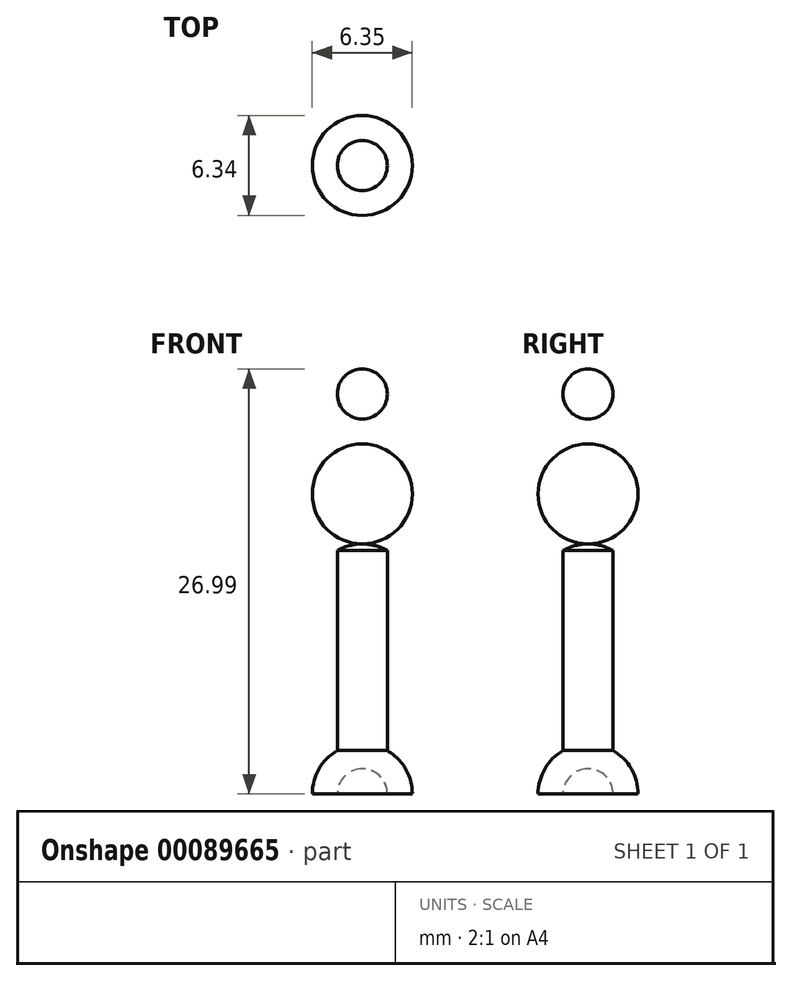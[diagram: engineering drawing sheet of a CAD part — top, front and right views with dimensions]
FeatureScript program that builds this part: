
annotation { "Feature Type Name" : "Feature", "Feature Type Description" : "" }
export const myFeature = defineFeature(function(context is Context, id is Id, definition is map)
    precondition{}
    {
        {
            var Q0;
            Q0=qCreatedBy(makeId("Front.planeOp"),FACE);
            var sketch = newSketch(context, id + "F0", { "sketchPlane" : qUnion([Q0])});
            skCircle(sketch, "E0", {"center": v(0, 0) * mm, "radius": 3.18 * mm});
            skCircle(sketch, "E1", {"center": v(0, 6.35) * mm, "radius": 3.18 * mm});
            skCircle(sketch, "E2", {"center": v(0, 12.7) * mm, "radius": 3.18 * mm});
            skCircle(sketch, "E3", {"center": v(0, 19.05) * mm, "radius": 3.18 * mm});
            skLineSegment(sketch, "E4", {"start": v(0, 22.22) * mm, "end": v(0, -3.18) * mm});
            skCircle(sketch, "E5", {"center": v(0, 25.4) * mm, "radius": 1.59 * mm});
            skLineSegment(sketch, "E6", {"start": v(0, 25.4) * mm, "end": v(0, 0) * mm});
            skLineSegment(sketch, "E7.bottom", {"start": v(1.59, 0) * mm, "end": v(-1.59, 0) * mm});
            skLineSegment(sketch, "E7.top", {"start": v(1.59, 25.4) * mm, "end": v(-1.59, 25.4) * mm});
            skLineSegment(sketch, "E7.left", {"start": v(1.59, 0) * mm, "end": v(1.59, 25.4) * mm});
            skLineSegment(sketch, "E7.right", {"start": v(-1.59, 0) * mm, "end": v(-1.59, 25.4) * mm});
            skCircle(sketch, "E8", {"center": v(0, 0) * mm, "radius": 1.59 * mm});
            skLineSegment(sketch, "E9", {"start": v(0, 25.4) * mm, "end": v(0, 26.99) * mm});
            skLineSegment(sketch, "E10", {"start": v(1.59, 0) * mm, "end": v(3.18, 0) * mm});
            skSolve(sketch);
        }
        {
            var Q0;
            {var subQ0=sQuery(id+"F0.wireOp",EDGE,"E10");Q0=makeQuery(id+"F0.imprint","IMPRINT",FACE,{"disambiguationData":[TD([[makeQuery(id+"F0.imprint","IMPRINT",EDGE,{"derivedFrom":subQ0}),1.0]])]});}
            var Q1;
            {var subQ0=sQuery(id+"F0.wireOp",EDGE,"E7.left");var subQ1=sQuery(id+"F0.wireOp",EDGE,"E0");var subQ2=makeQuery(id+"F0.imprint","INTERSECT",VERTEX,{"derivedFrom":[subQ1,subQ0]});Q1=makeQuery(id+"F0.imprint","IMPRINT",FACE,{"disambiguationData":[TD([[makeQuery(id+"F0.imprint","IMPRINT",EDGE,{"disambiguationData":[TD([[subQ2,-1.0]])],"derivedFrom":subQ1}),1.0]])]});}
            var Q2;
            {var subQ0=sQuery(id+"F0.wireOp",EDGE,"E7.left");var subQ1=sQuery(id+"F0.wireOp",EDGE,"E0");var subQ2=makeQuery(id+"F0.imprint","INTERSECT",VERTEX,{"derivedFrom":[subQ1,subQ0]});Q2=makeQuery(id+"F0.imprint","IMPRINT",FACE,{"disambiguationData":[TD([[makeQuery(id+"F0.imprint","IMPRINT",EDGE,{"disambiguationData":[TD([[subQ2,-1.0]])],"derivedFrom":subQ0}),1.0]])]});}
            var Q3;
            {var subQ0=sQuery(id+"F0.wireOp",EDGE,"E7.left");var subQ1=sQuery(id+"F0.wireOp",EDGE,"E1");var subQ2=makeQuery(id+"F0.imprint","INTERSECT",VERTEX,{"disambiguationData":[OD(0.0)],"derivedFrom":[subQ1,subQ0]});Q3=makeQuery(id+"F0.imprint","IMPRINT",FACE,{"disambiguationData":[TD([[makeQuery(id+"F0.imprint","IMPRINT",EDGE,{"disambiguationData":[TD([[subQ2,1.0]])],"derivedFrom":subQ0}),1.0]])]});}
            var Q4;
            {var subQ0=sQuery(id+"F0.wireOp",EDGE,"E7.left");var subQ1=sQuery(id+"F0.wireOp",EDGE,"E1");var subQ2=makeQuery(id+"F0.imprint","INTERSECT",VERTEX,{"disambiguationData":[OD(0.0)],"derivedFrom":[subQ1,subQ0]});Q4=makeQuery(id+"F0.imprint","IMPRINT",FACE,{"disambiguationData":[TD([[makeQuery(id+"F0.imprint","IMPRINT",EDGE,{"disambiguationData":[TD([[subQ2,1.0]])],"derivedFrom":subQ1}),1.0]])]});}
            var Q5;
            {var subQ0=sQuery(id+"F0.wireOp",EDGE,"E7.left");var subQ1=sQuery(id+"F0.wireOp",EDGE,"E1");var subQ2=makeQuery(id+"F0.imprint","INTERSECT",VERTEX,{"disambiguationData":[OD(0.0)],"derivedFrom":[subQ1,subQ0]});Q5=makeQuery(id+"F0.imprint","IMPRINT",FACE,{"disambiguationData":[TD([[makeQuery(id+"F0.imprint","IMPRINT",EDGE,{"disambiguationData":[TD([[subQ2,-1.0]])],"derivedFrom":subQ0}),1.0]])]});}
            var Q6;
            {var subQ0=sQuery(id+"F0.wireOp",EDGE,"E7.left");var subQ1=sQuery(id+"F0.wireOp",EDGE,"E2");var subQ2=makeQuery(id+"F0.imprint","INTERSECT",VERTEX,{"disambiguationData":[OD(0.0)],"derivedFrom":[subQ1,subQ0]});Q6=makeQuery(id+"F0.imprint","IMPRINT",FACE,{"disambiguationData":[TD([[makeQuery(id+"F0.imprint","IMPRINT",EDGE,{"disambiguationData":[TD([[subQ2,1.0]])],"derivedFrom":subQ0}),1.0]])]});}
            var Q7;
            {var subQ0=sQuery(id+"F0.wireOp",EDGE,"E7.left");var subQ1=sQuery(id+"F0.wireOp",EDGE,"E2");var subQ2=makeQuery(id+"F0.imprint","INTERSECT",VERTEX,{"disambiguationData":[OD(0.0)],"derivedFrom":[subQ1,subQ0]});Q7=makeQuery(id+"F0.imprint","IMPRINT",FACE,{"disambiguationData":[TD([[makeQuery(id+"F0.imprint","IMPRINT",EDGE,{"disambiguationData":[TD([[subQ2,-1.0]])],"derivedFrom":subQ0}),1.0]])]});}
            var Q8;
            {var subQ0=sQuery(id+"F0.wireOp",EDGE,"E7.left");var subQ1=sQuery(id+"F0.wireOp",EDGE,"E3");var subQ2=makeQuery(id+"F0.imprint","INTERSECT",VERTEX,{"disambiguationData":[OD(0.0)],"derivedFrom":[subQ1,subQ0]});Q8=makeQuery(id+"F0.imprint","IMPRINT",FACE,{"disambiguationData":[TD([[makeQuery(id+"F0.imprint","IMPRINT",EDGE,{"disambiguationData":[TD([[subQ2,-1.0]])],"derivedFrom":subQ1}),1.0]])]});}
            var Q9;
            {var subQ0=sQuery(id+"F0.wireOp",EDGE,"E7.left");var subQ1=sQuery(id+"F0.wireOp",EDGE,"E3");var subQ2=makeQuery(id+"F0.imprint","INTERSECT",VERTEX,{"disambiguationData":[OD(0.0)],"derivedFrom":[subQ1,subQ0]});Q9=makeQuery(id+"F0.imprint","IMPRINT",FACE,{"disambiguationData":[TD([[makeQuery(id+"F0.imprint","IMPRINT",EDGE,{"disambiguationData":[TD([[subQ2,1.0]])],"derivedFrom":subQ1}),1.0]])]});}
            var Q10;
            {var subQ0=sQuery(id+"F0.wireOp",EDGE,"E7.left");var subQ1=sQuery(id+"F0.wireOp",EDGE,"E3");var subQ2=makeQuery(id+"F0.imprint","INTERSECT",VERTEX,{"disambiguationData":[OD(0.0)],"derivedFrom":[subQ1,subQ0]});Q10=makeQuery(id+"F0.imprint","IMPRINT",FACE,{"disambiguationData":[TD([[makeQuery(id+"F0.imprint","IMPRINT",EDGE,{"disambiguationData":[TD([[subQ2,-1.0]])],"derivedFrom":subQ1}),-1.0]])]});}
            var Q11;
            {var subQ1=sQuery(id+"F0.wireOp",EDGE,"E5");var subQ3=sQuery(id+"F0.wireOp",EDGE,"E6");var subQ4=makeQuery(id+"F0.imprint","INTERSECT",VERTEX,{"derivedFrom":[subQ1,subQ3]});Q11=makeQuery(id+"F0.imprint","IMPRINT",FACE,{"disambiguationData":[TD([[makeQuery(id+"F0.imprint","IMPRINT",EDGE,{"disambiguationData":[TD([[subQ4,-1.0]])],"derivedFrom":subQ1}),1.0]])]});}
            var Q12;
            {var subQ3=sQuery(id+"F0.wireOp",EDGE,"E9");Q12=makeQuery(id+"F0.imprint","IMPRINT",FACE,{"disambiguationData":[TD([[makeQuery(id+"F0.imprint","IMPRINT",EDGE,{"derivedFrom":subQ3}),-1.0]])]});}
            var Q13;
            {var subQ0=sQuery(id+"F0.wireOp",EDGE,"E7.left");var subQ1=sQuery(id+"F0.wireOp",EDGE,"E2");var subQ2=makeQuery(id+"F0.imprint","INTERSECT",VERTEX,{"disambiguationData":[OD(0.0)],"derivedFrom":[subQ1,subQ0]});Q13=makeQuery(id+"F0.imprint","IMPRINT",FACE,{"disambiguationData":[TD([[makeQuery(id+"F0.imprint","IMPRINT",EDGE,{"disambiguationData":[TD([[subQ2,1.0]])],"derivedFrom":subQ1}),1.0]])]});}
            var Q14;
            Q14=sQuery(id+"F0.wireOp",EDGE,"E6");
            revolve(context, id + "F1", {"entities" : qUnion([Q0, Q1, Q2, Q3, Q4, Q5, Q6, Q7, Q8, Q9, Q10, Q11, Q12, Q13]), "axis" : qUnion([Q14]), "revolveType" : RevolveType.FULL});
        }
    });
